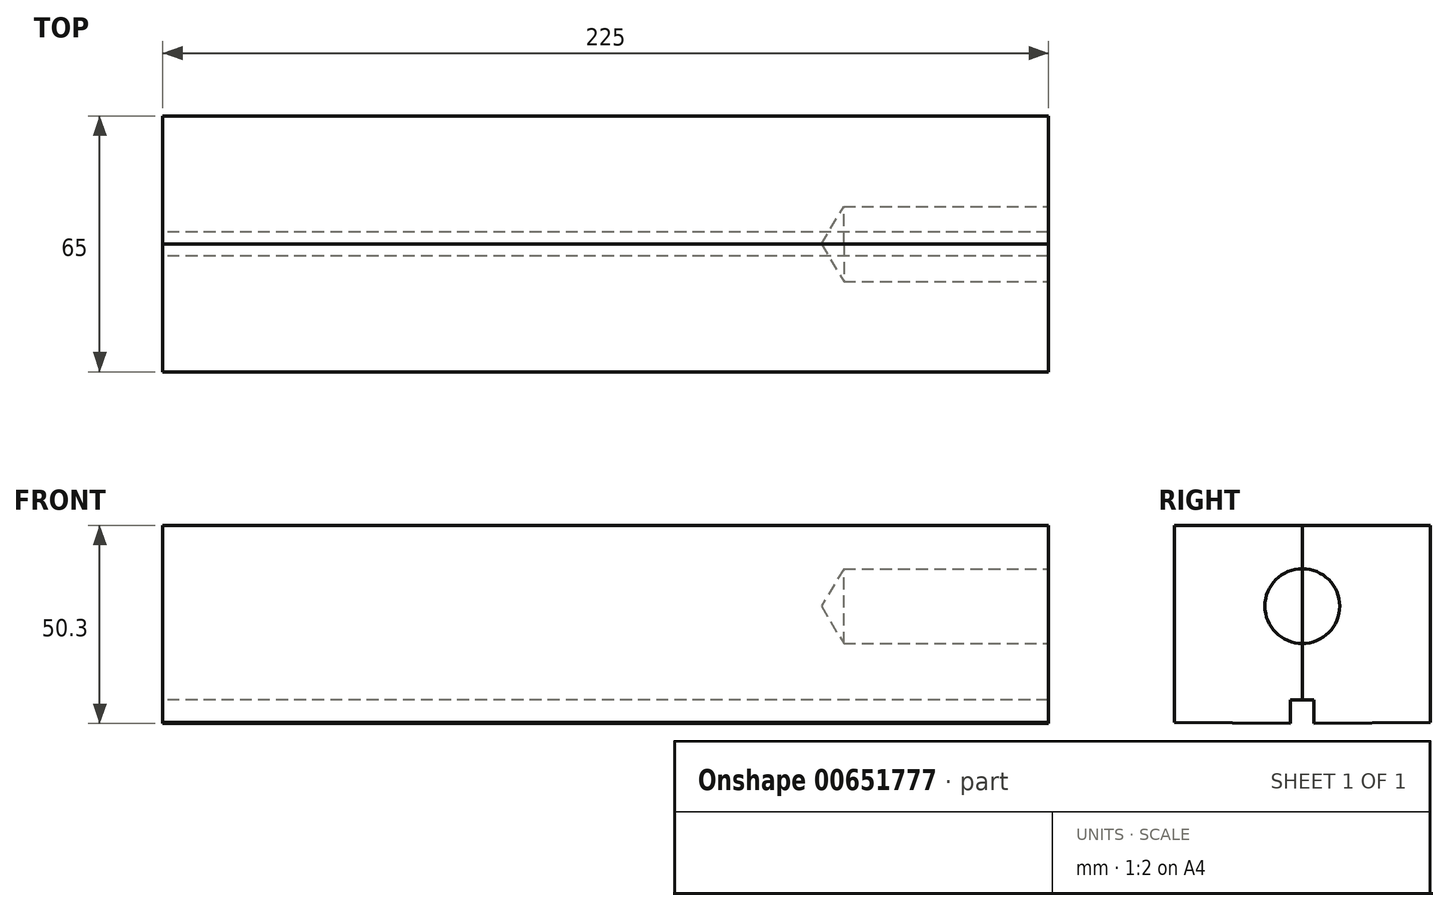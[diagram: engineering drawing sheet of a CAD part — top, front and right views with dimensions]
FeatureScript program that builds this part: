
annotation { "Feature Type Name" : "Feature", "Feature Type Description" : "" }
export const myFeature = defineFeature(function(context is Context, id is Id, definition is map)
    precondition{}
    {
        {
            var Q0;
            Q0=qCreatedBy(makeId("Right.planeOp"),FACE);
            var sketch = newSketch(context, id + "F0", { "sketchPlane" : qUnion([Q0])});
            skLineSegment(sketch, "E0", {"start": v(0, 5.67) * mm, "end": v(0, 50) * mm});
            skLineSegment(sketch, "E1", {"start": v(0, 50) * mm, "end": v(32.5, 50) * mm});
            skLineSegment(sketch, "E2", {"start": v(32.5, 50) * mm, "end": v(32.5, 0) * mm});
            skLineSegment(sketch, "E3", {"start": v(32.5, 0) * mm, "end": v(3, -0.3) * mm});
            skLineSegment(sketch, "E4", {"start": v(3, -0.3) * mm, "end": v(3, 5.7) * mm});
            skLineSegment(sketch, "E5", {"start": v(3, 5.7) * mm, "end": v(0, 5.67) * mm});
            skSolve(sketch);
        }
        {
            var Q0;
            Q0 = qSketchRegion(id + "F0", true);
            extrude(context, id + "F1", {"entities" : qUnion([Q0]), "depth" : 225 * mm, "offsetDistance" : 25 * mm});
        }
        {
            var Q0;
            Q0=makeQuery(id+"F1.opExtrude","CAP_FACE",FACE,{"disambiguationData":[OSD([sQuery(id+"F0.wireOp",EDGE,"E0"),sQuery(id+"F0.wireOp",EDGE,"E1"),sQuery(id+"F0.wireOp",EDGE,"E2"),sQuery(id+"F0.wireOp",EDGE,"E3"),sQuery(id+"F0.wireOp",EDGE,"E4"),sQuery(id+"F0.wireOp",EDGE,"E5")])],"isStart":false});
            var sketch = newSketch(context, id + "F2", { "sketchPlane" : qUnion([Q0])});
            skPoint(sketch, "E6", {"position": v(0, 29.5) * mm});
            skSolve(sketch);
        }
        {
            var Q0;
            Q0=sQuery(id+"F2.wireOp",VERTEX,"E6");
            var Q1;
            Q1=makeQuery(id+"F1.opExtrude","SWEPT_BODY",BODY,{"disambiguationData":[OSD([sQuery(id+"F0.wireOp",EDGE,"E0"),sQuery(id+"F0.wireOp",EDGE,"E1"),sQuery(id+"F0.wireOp",EDGE,"E2"),sQuery(id+"F0.wireOp",EDGE,"E3"),sQuery(id+"F0.wireOp",EDGE,"E4"),sQuery(id+"F0.wireOp",EDGE,"E5")])]});
            hole(context, id + "F3", {"style" : HoleStyle.SIMPLE, "endStyle" : HoleEndStyle.BLIND, "holeDiameter" : 19 * mm, "majorDiameter" : 5 * mm, "holeDepth" : 52 * mm, "isTappedThrough" : true, "tappedDepth" : 12 * mm, "tapClearance" : 3, "locations" : qUnion([Q0]), "scope" : qUnion([Q1])});
        }
        {
            var Q0;
            Q0=makeQuery(id+"F1.opExtrude","SWEPT_BODY",BODY,{"disambiguationData":[OSD([sQuery(id+"F0.wireOp",EDGE,"E0"),sQuery(id+"F0.wireOp",EDGE,"E1"),sQuery(id+"F0.wireOp",EDGE,"E2"),sQuery(id+"F0.wireOp",EDGE,"E3"),sQuery(id+"F0.wireOp",EDGE,"E4"),sQuery(id+"F0.wireOp",EDGE,"E5")])]});
            var Q1;
            Q1=makeQuery(id+"F1.opExtrude","SWEPT_FACE",FACE,{"disambiguationData":[OSD([sQuery(id+"F0.wireOp",EDGE,"E0")])]});
            mirror(context, id + "F4", {"entities" : qUnion([Q0]), "mirrorPlane" : qUnion([Q1])});
        }
    });
